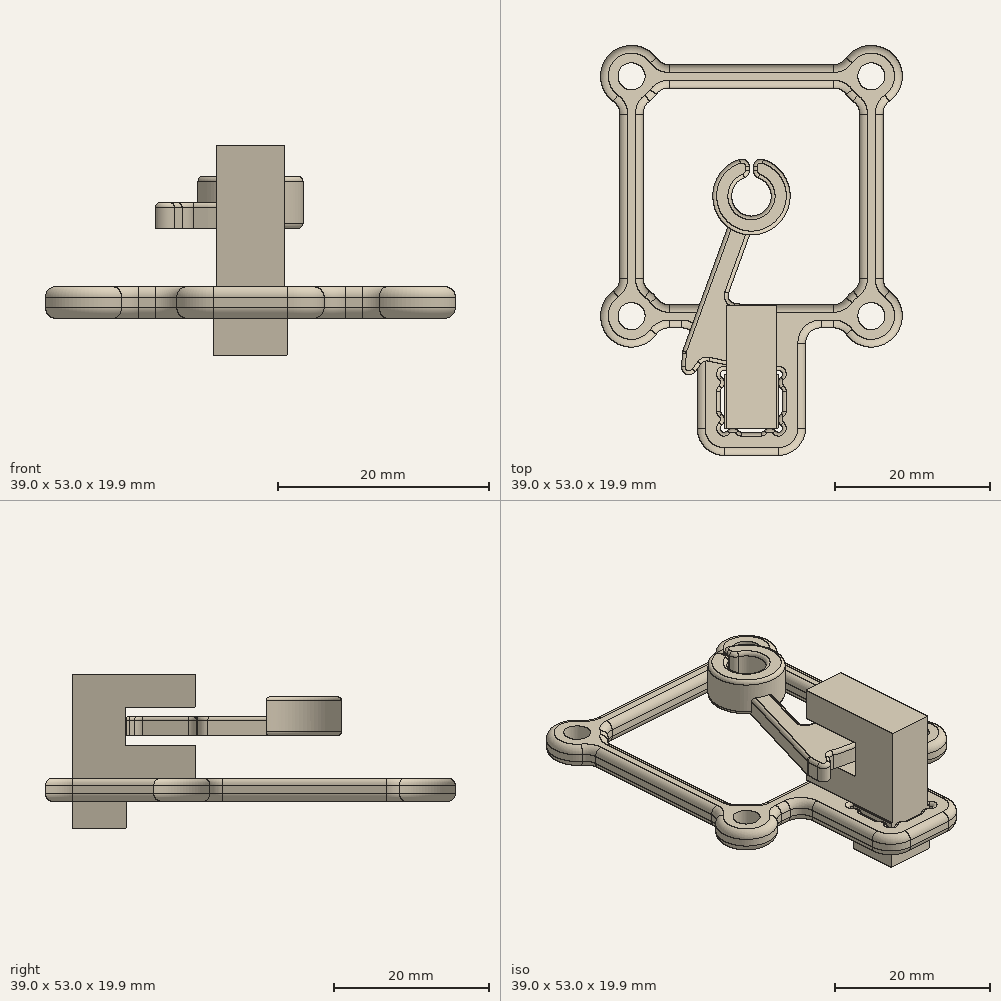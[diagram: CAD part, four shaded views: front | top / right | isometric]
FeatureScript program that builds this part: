
annotation { "Feature Type Name" : "Feature", "Feature Type Description" : "" }
export const myFeature = defineFeature(function(context is Context, id is Id, definition is map)
    precondition{}
    {
        {
            var Q0;
            Q0=qCreatedBy(makeId("Right.planeOp"),FACE);
            var sketch = newSketch(context, id + "F0", { "sketchPlane" : qUnion([Q0])});
            skLineSegment(sketch, "E0", {"start": v(-30, 3) * mm, "end": v(-14.1, 3) * mm});
            skLineSegment(sketch, "E1", {"start": v(-14.1, 3) * mm, "end": v(-14.1, 7.2) * mm});
            skLineSegment(sketch, "E2", {"start": v(-14.1, 7.2) * mm, "end": v(-23.1, 7.2) * mm});
            skLineSegment(sketch, "E3", {"start": v(-23.1, 7.2) * mm, "end": v(-23.1, 12.2) * mm});
            skLineSegment(sketch, "E4", {"start": v(-23.1, 12.2) * mm, "end": v(-14.1, 12.2) * mm});
            skLineSegment(sketch, "E5", {"start": v(-14.1, 12.2) * mm, "end": v(-14.1, 16.4) * mm});
            skLineSegment(sketch, "E6", {"start": v(-14.1, 16.4) * mm, "end": v(-30, 16.4) * mm});
            skLineSegment(sketch, "E7", {"start": v(-30, 16.4) * mm, "end": v(-30, 3) * mm});
            skLineSegment(sketch, "E8", {"start": v(-17, 12.2) * mm, "end": v(-17, 7.2) * mm, "construction": true});
            skSolve(sketch);
        }
        {
            var Q0;
            Q0 = qSketchRegion(id + "F0", true);
            extrude(context, id + "F1", {"entities" : qUnion([Q0]), "endBound" : BoundingType.SYMMETRIC, "depth" : 6.4 * mm, "offsetDistance" : 25 * mm});
        }
        {
            var Q0;
            Q0=makeQuery(id+"F1.opExtrude","SWEPT_FACE",FACE,{"disambiguationData":[OSD([sQuery(id+"F0.wireOp",EDGE,"E0")])]});
            var sketch = newSketch(context, id + "F2", { "sketchPlane" : qUnion([Q0])});
            skPoint(sketch, "E9.firstSnap0", {"position": v(0, 30) * mm});
            skLineSegment(sketch, "E9.bottom", {"start": v(-3.5, 30) * mm, "end": v(3.5, 30) * mm});
            skLineSegment(sketch, "E9.top", {"start": v(-3.5, 23) * mm, "end": v(3.5, 23) * mm});
            skLineSegment(sketch, "E9.left", {"start": v(-3.5, 30) * mm, "end": v(-3.5, 23) * mm});
            skLineSegment(sketch, "E9.right", {"start": v(3.5, 30) * mm, "end": v(3.5, 23) * mm});
            skSolve(sketch);
        }
        {
            var Q0;
            Q0 = qSketchRegion(id + "F2", true);
            extrude(context, id + "F3", {"entities" : qUnion([Q0]), "operationType" : NewBodyOperationType.ADD, "depth" : 6.5 * mm, "offsetDistance" : 25 * mm});
        }
        {
            var Q0;
            Q0=qCreatedBy(makeId("Top.planeOp"),FACE);
            var sketch = newSketch(context, id + "F4", { "sketchPlane" : qUnion([Q0])});
            skLineSegment(sketch, "E10", {"start": v(15.5, -15.5) * mm, "end": v(15.5, 0) * mm, "construction": true});
            skLineSegment(sketch, "E11", {"start": v(17, -11.8) * mm, "end": v(17, 0) * mm});
            skLineSegment(sketch, "E12.MirrorCS", {"start": v(11.8, 17) * mm, "end": v(0, 17) * mm});
            skLineSegment(sketch, "E13.MirrorCS", {"start": v(17, 11.8) * mm, "end": v(17, 0) * mm});
            skLineSegment(sketch, "E14.MirrorCS", {"start": v(-17, -11.8) * mm, "end": v(-17, 0) * mm});
            skLineSegment(sketch, "E15.MirrorCS", {"start": v(-17, 11.8) * mm, "end": v(-17, 0) * mm});
            skLineSegment(sketch, "E16.MirrorCS", {"start": v(-11.8, 17) * mm, "end": v(0, 17) * mm});
            skCircle(sketch, "E17", {"center": v(15.5, -15.5) * mm, "radius": 1.75 * mm});
            skCircle(sketch, "E18.MirrorC", {"center": v(15.5, 15.5) * mm, "radius": 1.75 * mm});
            skCircle(sketch, "E19.MirrorC", {"center": v(-15.5, 15.5) * mm, "radius": 1.75 * mm});
            skCircle(sketch, "E20.MirrorC", {"center": v(-15.5, -15.5) * mm, "radius": 1.75 * mm});
            skArc(sketch, "E21", {"start": v(17, 11.8) * mm, "mid": v(18.33, 18.33) * mm, "end": v(11.8, 17) * mm});
            skArc(sketch, "E22.MirrorCS", {"start": v(-17, 11.8) * mm, "mid": v(-18.33, 18.33) * mm, "end": v(-11.8, 17) * mm});
            skLineSegment(sketch, "E23", {"start": v(14, 0) * mm, "end": v(14, -11.8) * mm});
            skLineSegment(sketch, "E24.MirrorCS", {"start": v(0, -14) * mm, "end": v(11.8, -14) * mm});
            skArc(sketch, "E25", {"start": v(11.8, -17) * mm, "mid": v(18.33, -18.33) * mm, "end": v(17, -11.8) * mm});
            skArc(sketch, "E26.trimOffspring", {"start": v(14, -11.8) * mm, "mid": v(12.67, -12.67) * mm, "end": v(11.8, -14) * mm});
            skLineSegment(sketch, "E27.MirrorCS", {"start": v(0, -14) * mm, "end": v(-11.8, -14) * mm});
            skArc(sketch, "E28.MirrorCS", {"start": v(-14, -11.8) * mm, "mid": v(-12.67, -12.67) * mm, "end": v(-11.8, -14) * mm});
            skLineSegment(sketch, "E29.MirrorCS", {"start": v(-14, 0) * mm, "end": v(-14, -11.8) * mm});
            skArc(sketch, "E30.MirrorCS", {"start": v(-11.8, -17) * mm, "mid": v(-18.33, -18.33) * mm, "end": v(-17, -11.8) * mm});
            skLineSegment(sketch, "E31.MirrorCS", {"start": v(-14, 0) * mm, "end": v(-14, 11.8) * mm});
            skArc(sketch, "E32.MirrorCS", {"start": v(-14, 11.8) * mm, "mid": v(-12.67, 12.67) * mm, "end": v(-11.8, 14) * mm});
            skLineSegment(sketch, "E33.MirrorCS", {"start": v(0, 14) * mm, "end": v(-11.8, 14) * mm});
            skLineSegment(sketch, "E34.MirrorCS", {"start": v(0, 14) * mm, "end": v(11.8, 14) * mm});
            skArc(sketch, "E35.MirrorCS", {"start": v(14, 11.8) * mm, "mid": v(12.67, 12.67) * mm, "end": v(11.8, 14) * mm});
            skLineSegment(sketch, "E36.MirrorCS", {"start": v(14, 0) * mm, "end": v(14, 11.8) * mm});
            skArc(sketch, "E37", {"start": v(3.83, -23.37) * mm, "mid": v(3.85, -22.65) * mm, "end": v(3.13, -22.67) * mm});
            skArc(sketch, "E38", {"start": v(3.83, -23.37) * mm, "mid": v(3.5, -24.12) * mm, "end": v(3.83, -24.86) * mm});
            skArc(sketch, "E39", {"start": v(4, -25.24) * mm, "mid": v(3.96, -25.03) * mm, "end": v(3.83, -24.86) * mm});
            skArc(sketch, "E40", {"start": v(1.64, -22.67) * mm, "mid": v(2.38, -23) * mm, "end": v(3.13, -22.67) * mm});
            skArc(sketch, "E41", {"start": v(1.64, -22.67) * mm, "mid": v(1.47, -22.54) * mm, "end": v(1.26, -22.5) * mm});
            skLineSegment(sketch, "E42", {"start": v(0, -22.5) * mm, "end": v(1.26, -22.5) * mm});
            skLineSegment(sketch, "E43.trimOffspring", {"start": v(4, -25.24) * mm, "end": v(4, -27.76) * mm});
            skArc(sketch, "E44", {"start": v(3.83, -28.14) * mm, "mid": v(3.96, -27.97) * mm, "end": v(4, -27.76) * mm});
            skArc(sketch, "E45", {"start": v(3.13, -30.33) * mm, "mid": v(3.85, -30.35) * mm, "end": v(3.83, -29.63) * mm});
            skArc(sketch, "E46", {"start": v(1.26, -30.5) * mm, "mid": v(1.47, -30.46) * mm, "end": v(1.64, -30.33) * mm});
            skArc(sketch, "E47", {"start": v(3.13, -30.33) * mm, "mid": v(2.38, -30) * mm, "end": v(1.64, -30.33) * mm});
            skArc(sketch, "E48", {"start": v(3.83, -28.14) * mm, "mid": v(3.5, -28.88) * mm, "end": v(3.83, -29.63) * mm});
            skLineSegment(sketch, "E49", {"start": v(1.26, -30.5) * mm, "end": v(0, -30.5) * mm});
            skLineSegment(sketch, "E50.MirrorCS", {"start": v(-1.26, -30.5) * mm, "end": v(0, -30.5) * mm});
            skArc(sketch, "E51.MirrorCS", {"start": v(-1.26, -30.5) * mm, "mid": v(-1.47, -30.46) * mm, "end": v(-1.64, -30.33) * mm});
            skArc(sketch, "E52.MirrorCS", {"start": v(-3.13, -30.33) * mm, "mid": v(-2.38, -30) * mm, "end": v(-1.64, -30.33) * mm});
            skArc(sketch, "E53.MirrorCS", {"start": v(-3.13, -30.33) * mm, "mid": v(-3.85, -30.35) * mm, "end": v(-3.83, -29.63) * mm});
            skArc(sketch, "E54.MirrorCS", {"start": v(-3.83, -28.14) * mm, "mid": v(-3.5, -28.88) * mm, "end": v(-3.83, -29.63) * mm});
            skArc(sketch, "E55.MirrorCS", {"start": v(-3.83, -28.14) * mm, "mid": v(-3.96, -27.97) * mm, "end": v(-4, -27.76) * mm});
            skLineSegment(sketch, "E56.MirrorCS", {"start": v(-4, -25.24) * mm, "end": v(-4, -27.76) * mm});
            skArc(sketch, "E57.MirrorCS", {"start": v(-4, -25.24) * mm, "mid": v(-3.96, -25.03) * mm, "end": v(-3.83, -24.86) * mm});
            skArc(sketch, "E58.MirrorCS", {"start": v(-3.83, -23.37) * mm, "mid": v(-3.5, -24.12) * mm, "end": v(-3.83, -24.86) * mm});
            skArc(sketch, "E59.MirrorCS", {"start": v(-3.83, -23.37) * mm, "mid": v(-3.85, -22.65) * mm, "end": v(-3.13, -22.67) * mm});
            skArc(sketch, "E60.MirrorCS", {"start": v(-1.64, -22.67) * mm, "mid": v(-2.38, -23) * mm, "end": v(-3.13, -22.67) * mm});
            skArc(sketch, "E61.MirrorCS", {"start": v(-1.64, -22.67) * mm, "mid": v(-1.47, -22.54) * mm, "end": v(-1.26, -22.5) * mm});
            skLineSegment(sketch, "E62.MirrorCS", {"start": v(0, -22.5) * mm, "end": v(-1.26, -22.5) * mm});
            skArc(sketch, "E63", {"start": v(3.5, -33.5) * mm, "mid": v(5.97, -32.47) * mm, "end": v(7, -30) * mm});
            skLineSegment(sketch, "E64", {"start": v(0, -33.5) * mm, "end": v(3.5, -33.5) * mm});
            skLineSegment(sketch, "E65.MirrorCS", {"start": v(0, -33.5) * mm, "end": v(-3.5, -33.5) * mm});
            skArc(sketch, "E66.MirrorCS", {"start": v(-3.5, -33.5) * mm, "mid": v(-5.97, -32.47) * mm, "end": v(-7, -30) * mm});
            skLineSegment(sketch, "E67", {"start": v(7, -17) * mm, "end": v(11.8, -17) * mm});
            skLineSegment(sketch, "E68", {"start": v(7, -30) * mm, "end": v(7, -17) * mm});
            skLineSegment(sketch, "E69", {"start": v(15.5, -15.5) * mm, "end": v(0, -15.5) * mm, "construction": true});
            skLineSegment(sketch, "E70.MirrorCS", {"start": v(-7, -30) * mm, "end": v(-7, -17) * mm});
            skLineSegment(sketch, "E71.MirrorCS", {"start": v(-7, -17) * mm, "end": v(-11.8, -17) * mm});
            skSolve(sketch);
        }
        {
            var Q0;
            Q0 = qSketchRegion(id + "F4", true);
            extrude(context, id + "F5", {"entities" : qUnion([Q0]), "depth" : 3 * mm, "offsetDistance" : 25 * mm});
        }
        {
            var Q0;
            Q0=makeQuery(id+"F5.opExtrude","SWEPT_EDGE",EDGE,{"disambiguationData":[OSD([sQuery(id+"F4.wireOp",EDGE,"a8555735-26c3-4f65-a860-25f75162539b0.MirrorCS"),sQuery(id+"F4.wireOp",EDGE,"0799e50e-ceb0-4bc4-bbe5-538137cfda140.MirrorCS")])]});
            var Q1;
            Q1=makeQuery(id+"F5.opExtrude","SWEPT_EDGE",EDGE,{"disambiguationData":[OSD([sQuery(id+"F4.wireOp",EDGE,"a8555735-26c3-4f65-a860-25f75162539b0.MirrorCS"),sQuery(id+"F4.wireOp",EDGE,"64177712-7b3a-44a6-aa49-8fedb9ba00d20.MirrorCS")])]});
            var Q2;
            Q2=makeQuery(id+"F5.opExtrude","SWEPT_EDGE",EDGE,{"disambiguationData":[OSD([sQuery(id+"F4.wireOp",EDGE,"8dbc9f53-56e3-4daa-b2e6-18b372a601fd0.MirrorCS"),sQuery(id+"F4.wireOp",EDGE,"64177712-7b3a-44a6-aa49-8fedb9ba00d20.MirrorCS")])]});
            var Q3;
            Q3=makeQuery(id+"F5.opExtrude","SWEPT_EDGE",EDGE,{"disambiguationData":[OSD([sQuery(id+"F4.wireOp",EDGE,"a9d5bc1a-3f45-466f-a3d1-f9c5c8bc7b320.MirrorCS"),sQuery(id+"F4.wireOp",EDGE,"8dbc9f53-56e3-4daa-b2e6-18b372a601fd0.MirrorCS")])]});
            var Q4;
            Q4=makeQuery(id+"F5.opExtrude","SWEPT_EDGE",EDGE,{"disambiguationData":[OSD([sQuery(id+"F4.wireOp",EDGE,"a9d5bc1a-3f45-466f-a3d1-f9c5c8bc7b320.MirrorCS"),sQuery(id+"F4.wireOp",EDGE,"b1453875-83ca-4b5f-a574-4d512ba434e60.MirrorCS")])]});
            var Q5;
            Q5=makeQuery(id+"F5.opExtrude","SWEPT_EDGE",EDGE,{"disambiguationData":[OSD([sQuery(id+"F4.wireOp",EDGE,"b1453875-83ca-4b5f-a574-4d512ba434e60.MirrorCS"),sQuery(id+"F4.wireOp",EDGE,"0799e50e-ceb0-4bc4-bbe5-538137cfda140.MirrorCS")])]});
            var Q6;
            Q6=makeQuery(id+"F5.opExtrude","SWEPT_EDGE",EDGE,{"disambiguationData":[OSD([sQuery(id+"F4.wireOp",EDGE,"e7409fc7-6dc5-4fa0-8bd2-797b179d6c2c0.MirrorCS"),sQuery(id+"F4.wireOp",EDGE,"M9usMHV9-M5Mz-yZaN-KI69-7Ii37aOQtZIX")])]});
            var Q7;
            Q7=makeQuery(id+"F5.opExtrude","SWEPT_EDGE",EDGE,{"disambiguationData":[OSD([sQuery(id+"F4.wireOp",EDGE,"aTV4rMBG-IH5X-uj4n-qkJM-fFTUkBYGj4x2"),sQuery(id+"F4.wireOp",EDGE,"M9usMHV9-M5Mz-yZaN-KI69-7Ii37aOQtZIX")])]});
            var Q8;
            Q8=makeQuery(id+"F5.opExtrude","SWEPT_EDGE",EDGE,{"disambiguationData":[OSD([sQuery(id+"F4.wireOp",EDGE,"PTNrz6NI-mq5m-TNIv-Xi8x-VQy7vNPVacqY"),sQuery(id+"F4.wireOp",EDGE,"aTV4rMBG-IH5X-uj4n-qkJM-fFTUkBYGj4x2")])]});
            var Q9;
            Q9=makeQuery(id+"F5.opExtrude","SWEPT_EDGE",EDGE,{"disambiguationData":[OSD([sQuery(id+"F4.wireOp",EDGE,"PTNrz6NI-mq5m-TNIv-Xi8x-VQy7vNPVacqY"),sQuery(id+"F4.wireOp",EDGE,"21tsBSvF-8sUR-DCw7-SQp4-mvLXMKqhCHSD")])]});
            var Q10;
            Q10=makeQuery(id+"F5.opExtrude","SWEPT_EDGE",EDGE,{"disambiguationData":[OSD([sQuery(id+"F4.wireOp",EDGE,"e7409fc7-6dc5-4fa0-8bd2-797b179d6c2c0.MirrorCS"),sQuery(id+"F4.wireOp",EDGE,"g1yxYMWX-jt1l-3A86-sZKU-5Gny3wGCPKmH")])]});
            var Q11;
            Q11=makeQuery(id+"F5.opExtrude","SWEPT_EDGE",EDGE,{"disambiguationData":[OSD([sQuery(id+"F4.wireOp",EDGE,"21tsBSvF-8sUR-DCw7-SQp4-mvLXMKqhCHSD"),sQuery(id+"F4.wireOp",EDGE,"g1yxYMWX-jt1l-3A86-sZKU-5Gny3wGCPKmH")])]});
            var Q12;
            Q12=makeQuery(id+"F5.opExtrude","SWEPT_EDGE",EDGE,{"disambiguationData":[OSD([sQuery(id+"F4.wireOp",EDGE,"245dff81-a295-4b07-9008-421e9b7a53a00.MirrorCS"),sQuery(id+"F4.wireOp",EDGE,"c89ee1b2-0b78-4cbd-895f-fd323061577d0.MirrorCS")])]});
            var Q13;
            Q13=makeQuery(id+"F5.opExtrude","SWEPT_EDGE",EDGE,{"disambiguationData":[OSD([sQuery(id+"F4.wireOp",EDGE,"1e5d889c-e50f-462a-9eb7-923bfa9751ae0.MirrorCS"),sQuery(id+"F4.wireOp",EDGE,"245dff81-a295-4b07-9008-421e9b7a53a00.MirrorCS")])]});
            var Q14;
            Q14=makeQuery(id+"F5.opExtrude","SWEPT_EDGE",EDGE,{"disambiguationData":[OSD([sQuery(id+"F4.wireOp",EDGE,"d27616a2-7ba6-4396-9515-65ae395c259e0.MirrorCS"),sQuery(id+"F4.wireOp",EDGE,"1e5d889c-e50f-462a-9eb7-923bfa9751ae0.MirrorCS")])]});
            var Q15;
            Q15=makeQuery(id+"F5.opExtrude","SWEPT_EDGE",EDGE,{"disambiguationData":[OSD([sQuery(id+"F4.wireOp",EDGE,"NrdYKNgb-I1ZW-t4Z6-g58g-EeJU3syeOFSo"),sQuery(id+"F4.wireOp",EDGE,"970832f9-6b41-47e3-a8ba-0691d5801f67.trimOffspring")])]});
            var Q16;
            Q16=makeQuery(id+"F5.opExtrude","SWEPT_EDGE",EDGE,{"disambiguationData":[OSD([sQuery(id+"F4.wireOp",EDGE,"1SyO1Pwo-PifW-mIW4-rRCh-1AxtkwPCzY5k"),sQuery(id+"F4.wireOp",EDGE,"970832f9-6b41-47e3-a8ba-0691d5801f67.trimOffspring")])]});
            var Q17;
            Q17=makeQuery(id+"F5.opExtrude","SWEPT_EDGE",EDGE,{"disambiguationData":[OSD([sQuery(id+"F4.wireOp",EDGE,"1SyO1Pwo-PifW-mIW4-rRCh-1AxtkwPCzY5k"),sQuery(id+"F4.wireOp",EDGE,"0psZ6I7g-lBjv-eOku-uZ22-lASfzRSIX1uf")])]});
            var Q18;
            Q18=makeQuery(id+"F5.opExtrude","SWEPT_EDGE",EDGE,{"disambiguationData":[OSD([sQuery(id+"F4.wireOp",EDGE,"E11"),sQuery(id+"F4.wireOp",EDGE,"0psZ6I7g-lBjv-eOku-uZ22-lASfzRSIX1uf")])]});
            var Q19;
            Q19=makeQuery(id+"F5.opExtrude","SWEPT_EDGE",EDGE,{"disambiguationData":[OSD([sQuery(id+"F4.wireOp",EDGE,"E13.MirrorCS"),sQuery(id+"F4.wireOp",EDGE,"E21")])]});
            var Q20;
            Q20=makeQuery(id+"F5.opExtrude","SWEPT_EDGE",EDGE,{"disambiguationData":[OSD([sQuery(id+"F4.wireOp",EDGE,"E12.MirrorCS"),sQuery(id+"F4.wireOp",EDGE,"E21")])]});
            var Q21;
            Q21=makeQuery(id+"F5.opExtrude","SWEPT_EDGE",EDGE,{"disambiguationData":[OSD([sQuery(id+"F4.wireOp",EDGE,"E16.MirrorCS"),sQuery(id+"F4.wireOp",EDGE,"E22.MirrorCS")])]});
            var Q22;
            Q22=makeQuery(id+"F5.opExtrude","SWEPT_EDGE",EDGE,{"disambiguationData":[OSD([sQuery(id+"F4.wireOp",EDGE,"E15.MirrorCS"),sQuery(id+"F4.wireOp",EDGE,"E22.MirrorCS")])]});
            var Q23;
            Q23=makeQuery(id+"F5.opExtrude","SWEPT_EDGE",EDGE,{"disambiguationData":[OSD([sQuery(id+"F4.wireOp",EDGE,"E14.MirrorCS"),sQuery(id+"F4.wireOp",EDGE,"c89ee1b2-0b78-4cbd-895f-fd323061577d0.MirrorCS")])]});
            var Q24;
            Q24=makeQuery(id+"F5.opExtrude","SWEPT_EDGE",EDGE,{"disambiguationData":[OSD([sQuery(id+"F4.wireOp",EDGE,"E32.MirrorCS"),sQuery(id+"F4.wireOp",EDGE,"E33.MirrorCS")])]});
            var Q25;
            Q25=makeQuery(id+"F5.opExtrude","SWEPT_EDGE",EDGE,{"disambiguationData":[OSD([sQuery(id+"F4.wireOp",EDGE,"E34.MirrorCS"),sQuery(id+"F4.wireOp",EDGE,"E35.MirrorCS")])]});
            var Q26;
            Q26=makeQuery(id+"F5.opExtrude","SWEPT_EDGE",EDGE,{"disambiguationData":[OSD([sQuery(id+"F4.wireOp",EDGE,"E35.MirrorCS"),sQuery(id+"F4.wireOp",EDGE,"E36.MirrorCS")])]});
            var Q27;
            Q27=makeQuery(id+"F5.opExtrude","SWEPT_EDGE",EDGE,{"disambiguationData":[OSD([sQuery(id+"F4.wireOp",EDGE,"E23"),sQuery(id+"F4.wireOp",EDGE,"E26.trimOffspring")])]});
            var Q28;
            Q28=makeQuery(id+"F5.opExtrude","SWEPT_EDGE",EDGE,{"disambiguationData":[OSD([sQuery(id+"F4.wireOp",EDGE,"E24.MirrorCS"),sQuery(id+"F4.wireOp",EDGE,"E26.trimOffspring")])]});
            var Q29;
            Q29=makeQuery(id+"F5.opExtrude","SWEPT_EDGE",EDGE,{"disambiguationData":[OSD([sQuery(id+"F4.wireOp",EDGE,"E27.MirrorCS"),sQuery(id+"F4.wireOp",EDGE,"E28.MirrorCS")])]});
            var Q30;
            Q30=makeQuery(id+"F5.opExtrude","SWEPT_EDGE",EDGE,{"disambiguationData":[OSD([sQuery(id+"F4.wireOp",EDGE,"E28.MirrorCS"),sQuery(id+"F4.wireOp",EDGE,"E29.MirrorCS")])]});
            var Q31;
            Q31=makeQuery(id+"F5.opExtrude","SWEPT_EDGE",EDGE,{"disambiguationData":[OSD([sQuery(id+"F4.wireOp",EDGE,"E31.MirrorCS"),sQuery(id+"F4.wireOp",EDGE,"E32.MirrorCS")])]});
            var Q32;
            Q32=makeQuery(id+"F5.opExtrude","SWEPT_EDGE",EDGE,{"disambiguationData":[OSD([sQuery(id+"F4.wireOp",EDGE,"E30.MirrorCS"),sQuery(id+"F4.wireOp",EDGE,"E71.MirrorCS")])]});
            var Q33;
            Q33=makeQuery(id+"F5.opExtrude","SWEPT_EDGE",EDGE,{"disambiguationData":[OSD([sQuery(id+"F4.wireOp",EDGE,"E70.MirrorCS"),sQuery(id+"F4.wireOp",EDGE,"E71.MirrorCS")])]});
            var Q34;
            Q34=makeQuery(id+"F5.opExtrude","SWEPT_EDGE",EDGE,{"disambiguationData":[OSD([sQuery(id+"F4.wireOp",EDGE,"E67"),sQuery(id+"F4.wireOp",EDGE,"E68")])]});
            var Q35;
            Q35=makeQuery(id+"F5.opExtrude","SWEPT_EDGE",EDGE,{"disambiguationData":[OSD([sQuery(id+"F4.wireOp",EDGE,"E25"),sQuery(id+"F4.wireOp",EDGE,"E67")])]});
            fillet(context, id + "F6", {"entities" : qUnion([Q0, Q1, Q2, Q3, Q4, Q5, Q6, Q7, Q8, Q9, Q10, Q11, Q12, Q13, Q14, Q15, Q16, Q17, Q18, Q19, Q20, Q21, Q22, Q23, Q24, Q25, Q26, Q27, Q28, Q29, Q30, Q31, Q32, Q33, Q34, Q35]), "radius" : 2 * mm, "tangentPropagation" : true, "allowEdgeOverflow" : false});
        }
        {
            var Q0;
            Q0=makeQuery(id+"F5.opExtrude","CAP_EDGE",EDGE,{"disambiguationData":[OSD([sQuery(id+"F4.wireOp",EDGE,"E12.MirrorCS"),sQuery(id+"F4.wireOp",EDGE,"E16.MirrorCS")])],"isStart":true});
            var Q1;
            Q1=makeQuery(id+"F5.opExtrude","CAP_EDGE",EDGE,{"disambiguationData":[OSD([sQuery(id+"F4.wireOp",EDGE,"2bQvAH7K-tXxA-A9Lp-mSYO-7W2tMZWS53I9")])],"isStart":true});
            var Q2;
            Q2=makeQuery(id+"F5.opExtrude","CAP_EDGE",EDGE,{"disambiguationData":[OSD([sQuery(id+"F4.wireOp",EDGE,"a8555735-26c3-4f65-a860-25f75162539b0.MirrorCS")])],"isStart":true});
            var Q3;
            Q3=makeQuery(id+"F5.opExtrude","CAP_EDGE",EDGE,{"disambiguationData":[OSD([sQuery(id+"F4.wireOp",EDGE,"e7409fc7-6dc5-4fa0-8bd2-797b179d6c2c0.MirrorCS")])],"isStart":true});
            var Q4;
            Q4=makeQuery(id+"F5.opExtrude","CAP_EDGE",EDGE,{"disambiguationData":[OSD([sQuery(id+"F4.wireOp",EDGE,"E11"),sQuery(id+"F4.wireOp",EDGE,"E13.MirrorCS")])],"isStart":false});
            var Q5;
            Q5=makeQuery(id+"F5.opExtrude","CAP_EDGE",EDGE,{"disambiguationData":[OSD([sQuery(id+"F4.wireOp",EDGE,"2bQvAH7K-tXxA-A9Lp-mSYO-7W2tMZWS53I9")])],"isStart":false});
            var Q6;
            Q6=makeQuery(id+"F5.opExtrude","CAP_EDGE",EDGE,{"disambiguationData":[OSD([sQuery(id+"F4.wireOp",EDGE,"a8555735-26c3-4f65-a860-25f75162539b0.MirrorCS")])],"isStart":false});
            var Q7;
            Q7=makeQuery(id+"F5.opExtrude","CAP_EDGE",EDGE,{"disambiguationData":[OSD([sQuery(id+"F4.wireOp",EDGE,"e7409fc7-6dc5-4fa0-8bd2-797b179d6c2c0.MirrorCS")])],"isStart":false});
            var Q8;
            Q8=makeQuery(id+"F5.opExtrude","CAP_EDGE",EDGE,{"disambiguationData":[OSD([sQuery(id+"F4.wireOp",EDGE,"E33.MirrorCS"),sQuery(id+"F4.wireOp",EDGE,"E34.MirrorCS")])],"isStart":true});
            var Q9;
            Q9=makeQuery(id+"F5.opExtrude","CAP_EDGE",EDGE,{"disambiguationData":[OSD([sQuery(id+"F4.wireOp",EDGE,"E23"),sQuery(id+"F4.wireOp",EDGE,"E36.MirrorCS")])],"isStart":false});
            fillet(context, id + "F7", {"entities" : qUnion([Q0, Q1, Q2, Q3, Q4, Q5, Q6, Q7, Q8, Q9]), "radius" : 1 * mm, "tangentPropagation" : true, "allowEdgeOverflow" : false});
        }
        {
            var Q0;
            Q0=makeQuery(id+"F5.opExtrude","CAP_EDGE",EDGE,{"disambiguationData":[OSD([sQuery(id+"F4.wireOp",EDGE,"E42"),sQuery(id+"F4.wireOp",EDGE,"E62.MirrorCS")])],"isStart":false});
            var Q1;
            Q1=makeQuery(id+"F5.opExtrude","CAP_EDGE",EDGE,{"disambiguationData":[OSD([sQuery(id+"F4.wireOp",EDGE,"E49"),sQuery(id+"F4.wireOp",EDGE,"E50.MirrorCS")])],"isStart":true});
            fillet(context, id + "F8", {"entities" : qUnion([Q0, Q1]), "radius" : 0.5 * mm, "tangentPropagation" : true, "allowEdgeOverflow" : false});
        }
        {
            var Q0;
            Q0=qCreatedBy(makeId("Top.planeOp"),FACE);
            var sketch = newSketch(context, id + "F9", { "sketchPlane" : qUnion([Q0])});
            skLineSegment(sketch, "E72", {"start": v(0, -14) * mm, "end": v(0, -22) * mm});
            skArc(sketch, "E73", {"start": v(-0.25, 5) * mm, "mid": v(0, -5) * mm, "end": v(0.25, 5) * mm});
            skLineSegment(sketch, "E74", {"start": v(0, 0) * mm, "end": v(-9.23, -25.37) * mm, "construction": true});
            skLineSegment(sketch, "E75", {"start": v(-9.23, -25.37) * mm, "end": v(-6.1, -21.14) * mm});
            skLineSegment(sketch, "E76.MirrorCS", {"start": v(-9.23, -25.37) * mm, "end": v(-8.92, -20.11) * mm});
            skArc(sketch, "E77", {"start": v(-0.25, 2.54) * mm, "mid": v(0, -2.55) * mm, "end": v(0.25, 2.54) * mm});
            skArc(sketch, "E78.trimOffspring", {"start": v(-6.1, -21.14) * mm, "mid": v(-3.08, -21.78) * mm, "end": v(0, -22) * mm});
            skLineSegment(sketch, "E79", {"start": v(-8.92, -20.11) * mm, "end": v(-3.04, -3.97) * mm});
            skLineSegment(sketch, "E80", {"start": v(-0.22, -5) * mm, "end": v(-3.35, -13.6) * mm});
            skArc(sketch, "E81.trimOffspring", {"start": v(-3.35, -13.6) * mm, "mid": v(-1.69, -13.9) * mm, "end": v(0, -14) * mm});
            skLineSegment(sketch, "E82", {"start": v(-0.25, 5) * mm, "end": v(-0.25, 2.54) * mm});
            skLineSegment(sketch, "E83.MirrorCS", {"start": v(0.25, 5) * mm, "end": v(0.25, 2.54) * mm});
            skSolve(sketch);
        }
        {
            var Q0;
            {var subQ1=sQuery(id+"F9.wireOp",EDGE,"E72");Q0=makeQuery(id+"F9.imprint","IMPRINT",FACE,{"disambiguationData":[TD([[makeQuery(id+"F9.imprint","IMPRINT",EDGE,{"derivedFrom":subQ1}),-1.0]])]});}
            var Q1;
            Q1=makeQuery(id+"F9.imprint","IMPRINT",FACE,{"disambiguationData":[TD([[makeQuery(id+"F9.imprint","IMPRINT",EDGE,{"derivedFrom":sQuery(id+"F9.wireOp",EDGE,"aNGQbjMl-hA1y-Jher-y02K-tRtK2kKIgg7U")}),-1.0]])]});
            extrude(context, id + "F10", {"entities" : qUnion([Q0, Q1]), "depth" : 11 * mm, "offsetDistance" : 25 * mm, "hasSecondDirection" : true, "secondDirectionOppositeDirection" : true, "secondDirectionDepth" : -8.5 * mm});
        }
        {
            var Q0;
            Q0=makeQuery(id+"F9.imprint","IMPRINT",FACE,{"disambiguationData":[TD([[makeQuery(id+"F9.imprint","IMPRINT",EDGE,{"derivedFrom":sQuery(id+"F9.wireOp",EDGE,"E77")}),-1.0]])]});
            extrude(context, id + "F11", {"entities" : qUnion([Q0]), "operationType" : NewBodyOperationType.ADD, "depth" : 13.5 * mm, "offsetDistance" : 25 * mm, "hasSecondDirection" : true, "secondDirectionOppositeDirection" : true, "secondDirectionDepth" : -8.5 * mm});
        }
        {
            var Q0;
            Q0=makeQuery(id+"F10.opExtrude","CAP_EDGE",EDGE,{"disambiguationData":[OSD([sQuery(id+"F9.wireOp",EDGE,"E73")])],"isStart":false});
            var Q1;
            Q1=makeQuery(id+"F10.opExtrude","SWEPT_EDGE",EDGE,{"disambiguationData":[OSD([sQuery(id+"F9.wireOp",EDGE,"E73"),sQuery(id+"F9.wireOp",EDGE,"390b1940-eed5-4ced-b0f4-1e22c8afd8f30.MirrorCS")])]});
            var Q2;
            Q2=makeQuery(id+"F10.opExtrude","SWEPT_EDGE",EDGE,{"disambiguationData":[OSD([sQuery(id+"F9.wireOp",EDGE,"E72"),sQuery(id+"F9.wireOp",EDGE,"E73")])]});
            var Q3;
            Q3=makeQuery(id+"F10.opExtrude","SWEPT_EDGE",EDGE,{"disambiguationData":[OSD([sQuery(id+"F9.wireOp",EDGE,"E72"),sQuery(id+"F9.wireOp",EDGE,"E78.trimOffspring")])]});
            var Q4;
            Q4=makeQuery(id+"F10.opExtrude","SWEPT_EDGE",EDGE,{"disambiguationData":[OSD([sQuery(id+"F9.wireOp",EDGE,"9B8DqObQ-sLfW-7wbZ-K34G-9xFKFbUcy3Kj"),sQuery(id+"F9.wireOp",EDGE,"390b1940-eed5-4ced-b0f4-1e22c8afd8f30.MirrorCS")])]});
            var Q5;
            {var subQ0=sQuery(id+"F9.wireOp",EDGE,"9a5276c3-87a0-416d-b92b-00e18afd57a80.MirrorCS");var subQ1=sQuery(id+"F9.wireOp",EDGE,"E76.MirrorCS");var subQ2=sQuery(id+"F9.wireOp",EDGE,"9B8DqObQ-sLfW-7wbZ-K34G-9xFKFbUcy3Kj");Q5=makeQuery(id+"F11.boolean.opBoolean","MERGE",EDGE,{"derivedFrom":[makeQuery(id+"F10.opExtrude","SWEPT_EDGE",EDGE,{"disambiguationData":[OSD([subQ2,subQ1,subQ0])]}),makeQuery(id+"F11.opExtrude","SWEPT_EDGE",EDGE,{"disambiguationData":[OSD([subQ2,subQ1,subQ0])]})]});}
            var Q6;
            {var subQ0=sQuery(id+"F9.wireOp",EDGE,"E78.trimOffspring");var subQ1=sQuery(id+"F9.wireOp",EDGE,"E75");var subQ2=sQuery(id+"F9.wireOp",EDGE,"aNGQbjMl-hA1y-Jher-y02K-tRtK2kKIgg7U");Q6=makeQuery(id+"F11.boolean.opBoolean","MERGE",EDGE,{"derivedFrom":[makeQuery(id+"F10.opExtrude","SWEPT_EDGE",EDGE,{"disambiguationData":[OSD([subQ2,subQ1,subQ0])]}),makeQuery(id+"F11.opExtrude","SWEPT_EDGE",EDGE,{"disambiguationData":[OSD([subQ2,subQ1,subQ0])]})]});}
            var Q7;
            Q7=makeQuery(id+"F10.opExtrude","SWEPT_EDGE",EDGE,{"disambiguationData":[OSD([sQuery(id+"F9.wireOp",EDGE,"E80"),sQuery(id+"F9.wireOp",EDGE,"E81.trimOffspring")])]});
            var Q8;
            Q8=makeQuery(id+"F11.opExtrude","SWEPT_EDGE",EDGE,{"disambiguationData":[OSD([sQuery(id+"F9.wireOp",EDGE,"E73"),sQuery(id+"F9.wireOp",EDGE,"E82")])]});
            var Q9;
            Q9=makeQuery(id+"F11.opExtrude","SWEPT_EDGE",EDGE,{"disambiguationData":[OSD([sQuery(id+"F9.wireOp",EDGE,"E73"),sQuery(id+"F9.wireOp",EDGE,"E83.MirrorCS")])]});
            var Q10;
            Q10=makeQuery(id+"F11.opExtrude","SWEPT_EDGE",EDGE,{"disambiguationData":[OSD([sQuery(id+"F9.wireOp",EDGE,"E77"),sQuery(id+"F9.wireOp",EDGE,"E83.MirrorCS")])]});
            var Q11;
            Q11=makeQuery(id+"F11.opExtrude","SWEPT_EDGE",EDGE,{"disambiguationData":[OSD([sQuery(id+"F9.wireOp",EDGE,"E77"),sQuery(id+"F9.wireOp",EDGE,"E82")])]});
            fillet(context, id + "F12", {"entities" : qUnion([Q0, Q1, Q2, Q3, Q4, Q5, Q6, Q7, Q8, Q9, Q10, Q11]), "radius" : 1 * mm, "tangentPropagation" : true, "allowEdgeOverflow" : false});
        }
        {
            var Q0;
            Q0=makeQuery(id+"F11.opExtrude","SWEPT_EDGE",EDGE,{"disambiguationData":[OSD([sQuery(id+"F9.wireOp",EDGE,"E75"),sQuery(id+"F9.wireOp",EDGE,"E76.MirrorCS")])]});
            var Q1;
            Q1=makeQuery(id+"F11.boolean.opBoolean","SPLIT",EDGE,{"derivedFrom":makeQuery(id+"F11.opExtrude","SWEPT_EDGE",EDGE,{"disambiguationData":[OSD([sQuery(id+"F9.wireOp",EDGE,"9B8DqObQ-sLfW-7wbZ-K34G-9xFKFbUcy3Kj"),sQuery(id+"F9.wireOp",EDGE,"E76.MirrorCS"),sQuery(id+"F9.wireOp",EDGE,"9a5276c3-87a0-416d-b92b-00e18afd57a80.MirrorCS")])]})});
            var Q2;
            Q2=makeQuery(id+"F11.boolean.opBoolean","SPLIT",EDGE,{"derivedFrom":makeQuery(id+"F11.opExtrude","SWEPT_EDGE",EDGE,{"disambiguationData":[OSD([sQuery(id+"F9.wireOp",EDGE,"aNGQbjMl-hA1y-Jher-y02K-tRtK2kKIgg7U"),sQuery(id+"F9.wireOp",EDGE,"E75"),sQuery(id+"F9.wireOp",EDGE,"E78.trimOffspring")])]})});
            var Q3;
            Q3=makeQuery(id+"F11.opExtrude","SWEPT_EDGE",EDGE,{"disambiguationData":[OSD([sQuery(id+"F9.wireOp",EDGE,"aNGQbjMl-hA1y-Jher-y02K-tRtK2kKIgg7U"),sQuery(id+"F9.wireOp",EDGE,"iR4gSqZ8-1RnX-EOKf-6kKX-JXJfOHufQPIU")])]});
            var Q4;
            Q4=makeQuery(id+"F11.opExtrude","SWEPT_EDGE",EDGE,{"disambiguationData":[OSD([sQuery(id+"F9.wireOp",EDGE,"iR4gSqZ8-1RnX-EOKf-6kKX-JXJfOHufQPIU"),sQuery(id+"F9.wireOp",EDGE,"9a5276c3-87a0-416d-b92b-00e18afd57a80.MirrorCS")])]});
            var Q5;
            Q5=makeQuery(id+"F11.opExtrude","CAP_EDGE",EDGE,{"disambiguationData":[OSD([sQuery(id+"F9.wireOp",EDGE,"E73")])],"isStart":false});
            var Q6;
            Q6=makeQuery(id+"F11.opExtrude","CAP_EDGE",EDGE,{"disambiguationData":[OSD([sQuery(id+"F9.wireOp",EDGE,"E73")])],"isStart":true});
            fillet(context, id + "F13", {"entities" : qUnion([Q0, Q1, Q2, Q3, Q4, Q5, Q6]), "radius" : 0.5 * mm, "tangentPropagation" : true, "allowEdgeOverflow" : false});
        }
        {
            var Q0;
            Q0=makeQuery(id+"F11.opExtrude","CAP_EDGE",EDGE,{"disambiguationData":[OSD([sQuery(id+"F9.wireOp",EDGE,"9a5276c3-87a0-416d-b92b-00e18afd57a80.MirrorCS")])],"isStart":false});
            var Q1;
            Q1=makeQuery(id+"F10.opExtrude","CAP_EDGE",EDGE,{"disambiguationData":[OSD([sQuery(id+"F9.wireOp",EDGE,"9a5276c3-87a0-416d-b92b-00e18afd57a80.MirrorCS")])],"isStart":false});
            var Q2;
            Q2=makeQuery(id+"F10.opExtrude","CAP_EDGE",EDGE,{"disambiguationData":[OSD([sQuery(id+"F9.wireOp",EDGE,"9B8DqObQ-sLfW-7wbZ-K34G-9xFKFbUcy3Kj")])],"isStart":false});
            var Q3;
            Q3=makeQuery(id+"F10.opExtrude","CAP_EDGE",EDGE,{"disambiguationData":[OSD([sQuery(id+"F9.wireOp",EDGE,"E72")])],"isStart":false});
            fillet(context, id + "F14", {"entities" : qUnion([Q0, Q1, Q2, Q3]), "radius" : 0.5 * mm, "tangentPropagation" : true, "allowEdgeOverflow" : false});
        }
    });
